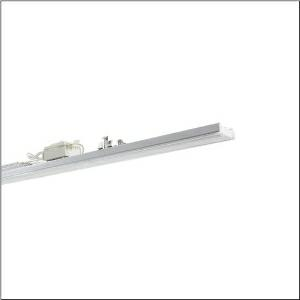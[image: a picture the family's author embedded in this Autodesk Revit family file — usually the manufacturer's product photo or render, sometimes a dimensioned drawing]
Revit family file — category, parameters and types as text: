
# Revit family: licross_11_recessed_mo_51te147n48xg
name_source: partatom
category: Lighting Fixtures
units: mm (PartAtom-declared; Revit-internal decimal feet)

## family parameters
Cut with Voids When Loaded = No
Host = Face
Light Source = No
Part Type = Normal
Room Calculation Point = No
Round Connector Dimension = Use Diameter
Shared = No

## types (1)
- Licross 11 Recessed MO (1 x LED, 8240 lm, 48.5 W, 4000K)
    Apparent Load = 49 VA
    CIE Flux Codes = 56 84 97 100 100
    Color Rendering = 80
    Color Temperature = 4000K
    Default Elevation = 1800 mm
    Description = Licross 11 Recessed MO, luminaire insert, of sheet steel, galvanised, coil coated, white, length: 1.500mm, width: 66mm, height: 67mm, LED rated luminous flux: 8.240lm, light colour: 840, SDCM (Standard Deviation of Colour Matching)MacAdam ≤ 2 SDCM (initial), control gear: ON/OFF, with plug, 3-pole, with phase selection, mains connection: 220..240V, AC, 50/60Hz, rated input power: 49W, internal wiring halogen-free, primary light control with lens, of plastic, primary optical cover: cover, of PMMA, light emission: direct distribution, primary light characteristic: asymmetric, protection rating (complete): IP54, insulation class (complete): insulation class I (protective earthing), certification: CE, ENEC, VDE, UKCA, protection symbol: D if used in an environment with non-conductive dust loads with corresponding accessories, impact resistance: IK06, permissible ambient temperature for indoor applications: -35..+35°C, corresponds to IFS (International Featured Standards) requirements for safety and quality in the food industry, reducing of maximum allowable ambient temperature of 5°C with ceiling mounting, The light source and the operating device comply with the requirements of the Ecodesign Regulation (EU) 2019/2020 and are replaceable in accordance with this regulation, packaging unit: 1 piece
    Height = 58 mm
    Lamp = 1 x LED
    Lamp Light Flux = 8240 lm
    Lamp Power = 48.5 W
    Lamp count = 1
    Length = 1500 mm
    Luminous efficacy = 170 lm/W
    Manufacturer = Siteco
    ModVariant = No
    Model = 51TE147N48XG
    Mounting Place = Ceiling
    Mounting Type = Pendant
    Number of Poles = 1
    OnlyDefault = Yes
    Power Factor = 1
    Product Name = Licross 11 Recessed MO
    Product group = luminaire insert | ceiling pendant
    ProductGroupID = 901
    Protection Class = Protection class I
    Protection Degree = IP 54
    RLX_Detail_Level = 1
    RLX_Emergency_Light_Flux = 0 lm
    RLX_Emergency_Type = 0
    RLX_Emergency_Type_DB = No
    RlxData = <blob elided: 21561 chars, md5=bb930f87>
    Socket = socket
    Standby Power = 0 W
    System Light Flux = 8240 lm
    System Power = 49 W
    Type Comments = Product without accessories
    Type Image = l_1296930.jpg
    URL = http://relux.com
    VarID = ---
    Voltage = 0 V
    Weight = 0.00 kg
    Width = 66 mm

## geometry (parser evidence)
native form markers: Blend x4, Sweep x12
no freeform markers — native parametric forms only
